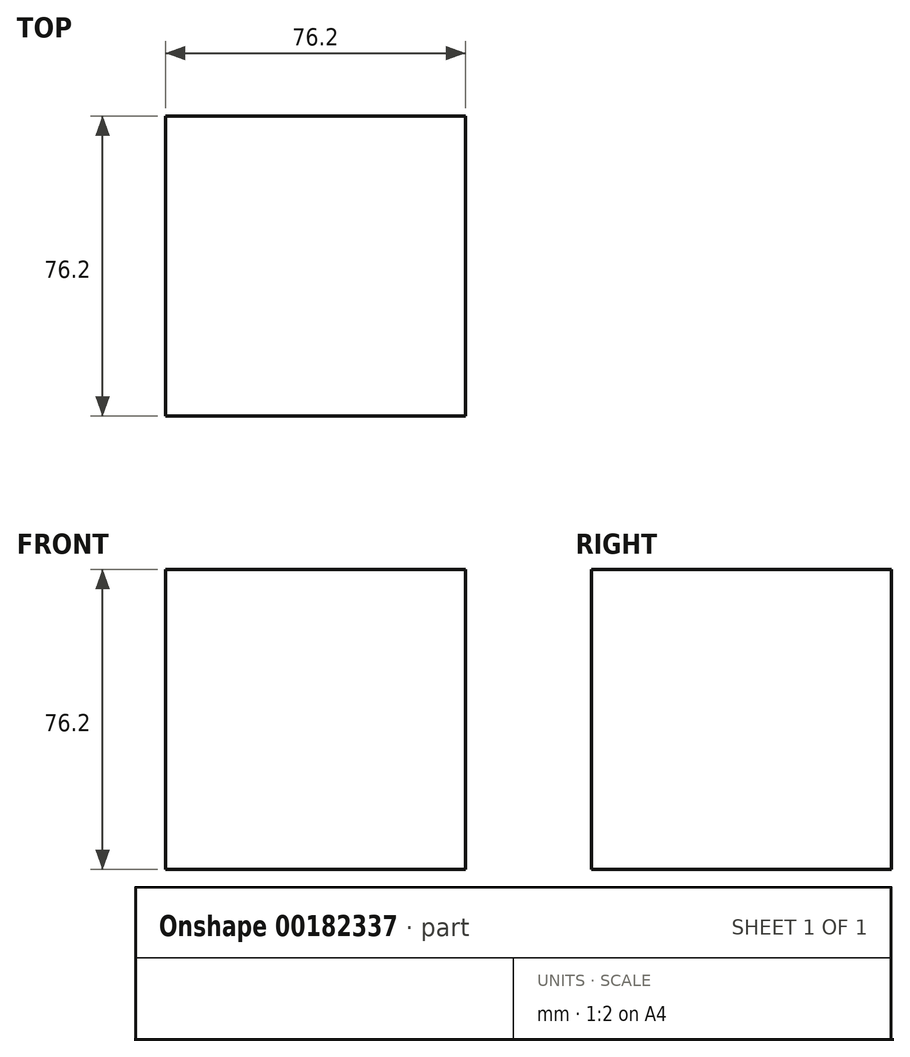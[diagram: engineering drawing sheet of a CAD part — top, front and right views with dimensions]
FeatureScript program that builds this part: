
annotation { "Feature Type Name" : "Feature", "Feature Type Description" : "" }
export const myFeature = defineFeature(function(context is Context, id is Id, definition is map)
    precondition{}
    {
        {
            var Q0;
            Q0=qCreatedBy(makeId("Front.planeOp"),FACE);
            var sketch = newSketch(context, id + "F0", { "sketchPlane" : qUnion([Q0])});
            skLineSegment(sketch, "E0", {"start": v(-28.74, 24.97) * mm, "end": v(-28.74, -51.23) * mm});
            skLineSegment(sketch, "E1", {"start": v(-28.74, -51.23) * mm, "end": v(47.46, -51.23) * mm});
            skLineSegment(sketch, "E2", {"start": v(47.46, -51.23) * mm, "end": v(47.46, 24.97) * mm});
            skLineSegment(sketch, "E3", {"start": v(47.46, 24.97) * mm, "end": v(-28.74, 24.97) * mm});
            skSolve(sketch);
        }
        {
            var Q0;
            Q0=makeQuery(id+"F0.imprint","IMPRINT",FACE,{"disambiguationData":[TD([[makeQuery(id+"F0.imprint","IMPRINT",EDGE,{"derivedFrom":sQuery(id+"F0.wireOp",EDGE,"E0")}),1.0]])]});
            extrude(context, id + "F1", {"entities" : qUnion([Q0]), "depth" : 76.2 * mm});
        }
    });
